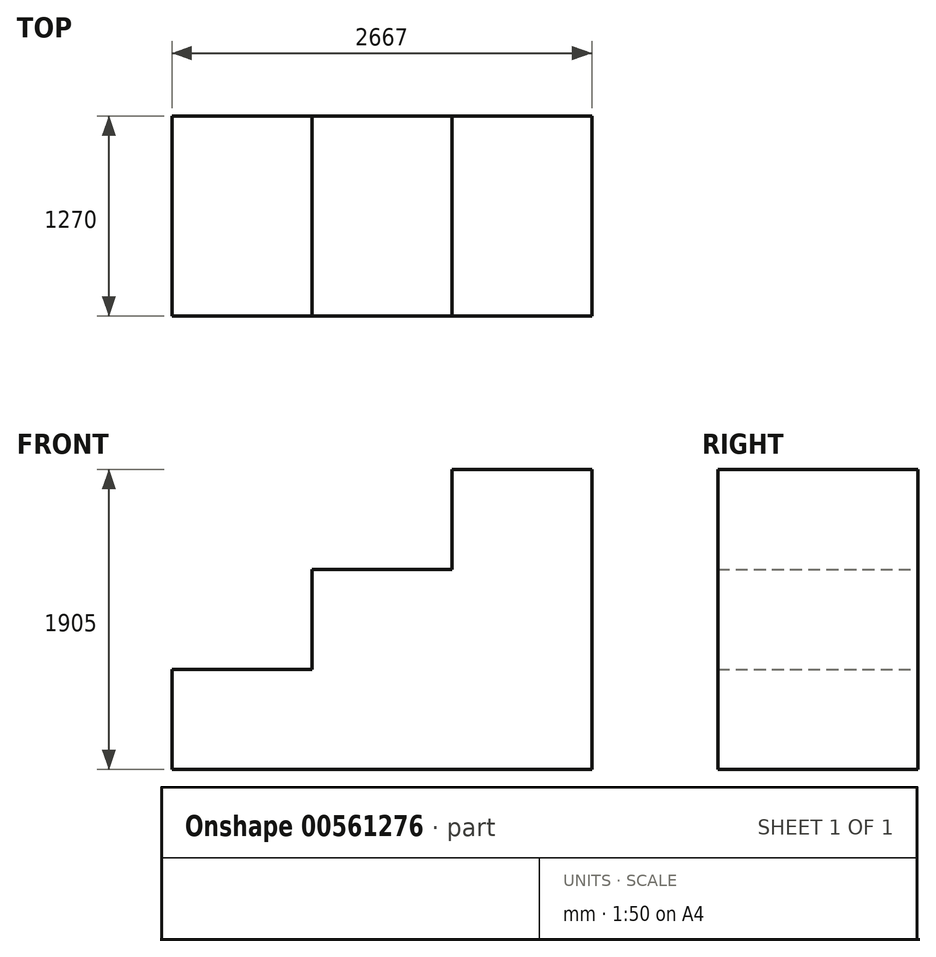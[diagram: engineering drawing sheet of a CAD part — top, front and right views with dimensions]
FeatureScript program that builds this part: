
annotation { "Feature Type Name" : "Feature", "Feature Type Description" : "" }
export const myFeature = defineFeature(function(context is Context, id is Id, definition is map)
    precondition{}
    {
        {
            var Q0;
            Q0=qCreatedBy(makeId("Front.planeOp"),FACE);
            var sketch = newSketch(context, id + "F0", { "sketchPlane" : qUnion([Q0])});
            skLineSegment(sketch, "E0", {"start": v(0, 0) * mm, "end": v(2667, 0) * mm});
            skLineSegment(sketch, "E1", {"start": v(2667, 0) * mm, "end": v(2667, 1905) * mm});
            skLineSegment(sketch, "E2", {"start": v(2667, 1905) * mm, "end": v(1778, 1905) * mm});
            skLineSegment(sketch, "E3", {"start": v(1778, 1905) * mm, "end": v(1778, 1270) * mm});
            skLineSegment(sketch, "E4", {"start": v(1778, 1270) * mm, "end": v(889, 1270) * mm});
            skLineSegment(sketch, "E5", {"start": v(889, 1270) * mm, "end": v(889, 635) * mm});
            skLineSegment(sketch, "E6", {"start": v(889, 635) * mm, "end": v(0, 635) * mm});
            skLineSegment(sketch, "E7", {"start": v(0, 635) * mm, "end": v(0, 0) * mm});
            skSolve(sketch);
        }
        {
            var Q0;
            Q0=makeQuery(id+"F0.imprint","IMPRINT",FACE,{"disambiguationData":[TD([[makeQuery(id+"F0.imprint","IMPRINT",EDGE,{"derivedFrom":sQuery(id+"F0.wireOp",EDGE,"E0")}),1.0]])]});
            extrude(context, id + "F1", {"entities" : qUnion([Q0]), "depth" : 1270 * mm, "offsetDistance" : 25.4 * mm});
        }
    });
